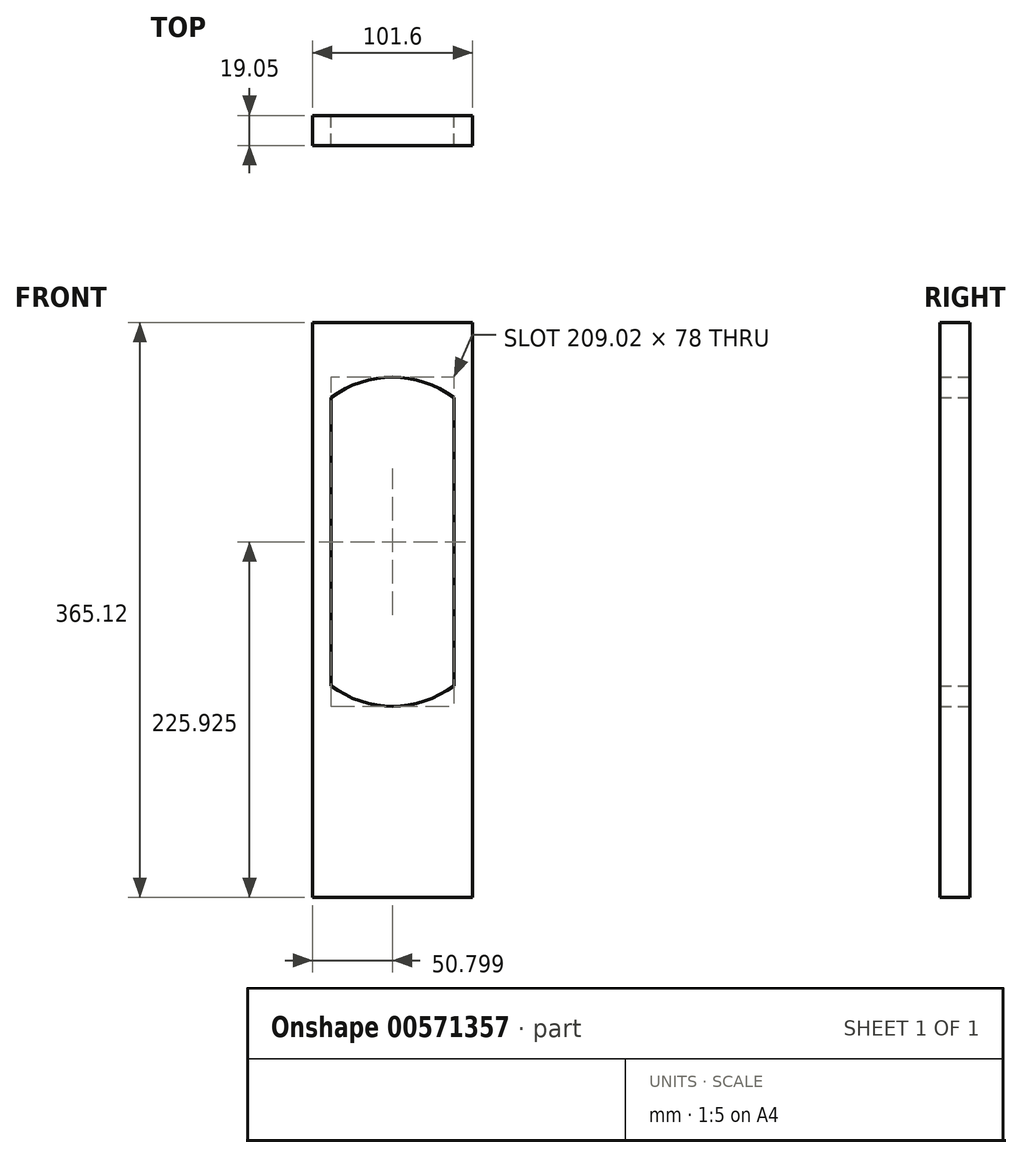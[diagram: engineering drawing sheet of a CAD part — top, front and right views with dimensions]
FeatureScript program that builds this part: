
annotation { "Feature Type Name" : "Feature", "Feature Type Description" : "" }
export const myFeature = defineFeature(function(context is Context, id is Id, definition is map)
    precondition{}
    {
        {
            var Q0;
            Q0=qCreatedBy(makeId("Front.planeOp"),FACE);
            var sketch = newSketch(context, id + "F0", { "sketchPlane" : qUnion([Q0])});
            skLineSegment(sketch, "E0", {"start": v(-163.86, -142.35) * mm, "end": v(-62.26, -142.35) * mm});
            skLineSegment(sketch, "E1", {"start": v(-163.86, -142.35) * mm, "end": v(-163.86, 222.77) * mm});
            skLineSegment(sketch, "E2", {"start": v(-62.26, -142.35) * mm, "end": v(-62.26, 222.77) * mm});
            skLineSegment(sketch, "E3", {"start": v(-163.86, 222.77) * mm, "end": v(-62.26, 222.77) * mm});
            skLineSegment(sketch, "E4", {"start": v(-113.06, 222.77) * mm, "end": v(-113.06, 38.62) * mm});
            skLineSegment(sketch, "E5", {"start": v(-113.06, 200.55) * mm, "end": v(-113.06, 200.55) * mm});
            skLineSegment(sketch, "E6", {"start": v(-113.06, 38.62) * mm, "end": v(-113.06, 38.62) * mm});
            skLineSegment(sketch, "E7", {"start": v(-113.06, 175.03) * mm, "end": v(-152.06, 175.03) * mm});
            skLineSegment(sketch, "E8", {"start": v(-113.06, 175.03) * mm, "end": v(-74.06, 175.03) * mm});
            skArc(sketch, "E9", {"start": v(-74.06, 175.03) * mm, "mid": v(-113.06, 188.09) * mm, "end": v(-152.06, 175.03) * mm});
            skLineSegment(sketch, "E10", {"start": v(-152.06, 175.03) * mm, "end": v(-152.06, -7.88) * mm});
            skLineSegment(sketch, "E11", {"start": v(-74.06, 175.03) * mm, "end": v(-74.06, -7.88) * mm});
            skLineSegment(sketch, "E12", {"start": v(-152.06, -7.88) * mm, "end": v(-74.06, -7.88) * mm});
            skArc(sketch, "E13", {"start": v(-152.06, -7.88) * mm, "mid": v(-113.06, -20.94) * mm, "end": v(-74.06, -7.88) * mm});
            skSolve(sketch);
        }
        {
            var Q0;
            Q0=makeQuery(id+"F0.imprint","IMPRINT",FACE,{"disambiguationData":[TD([[makeQuery(id+"F0.imprint","IMPRINT",EDGE,{"derivedFrom":sQuery(id+"F0.wireOp",EDGE,"E0")}),1.0]])]});
            extrude(context, id + "F1", {"entities" : qUnion([Q0]), "depth" : 19.05 * mm, "offsetDistance" : 25.4 * mm});
        }
    });
